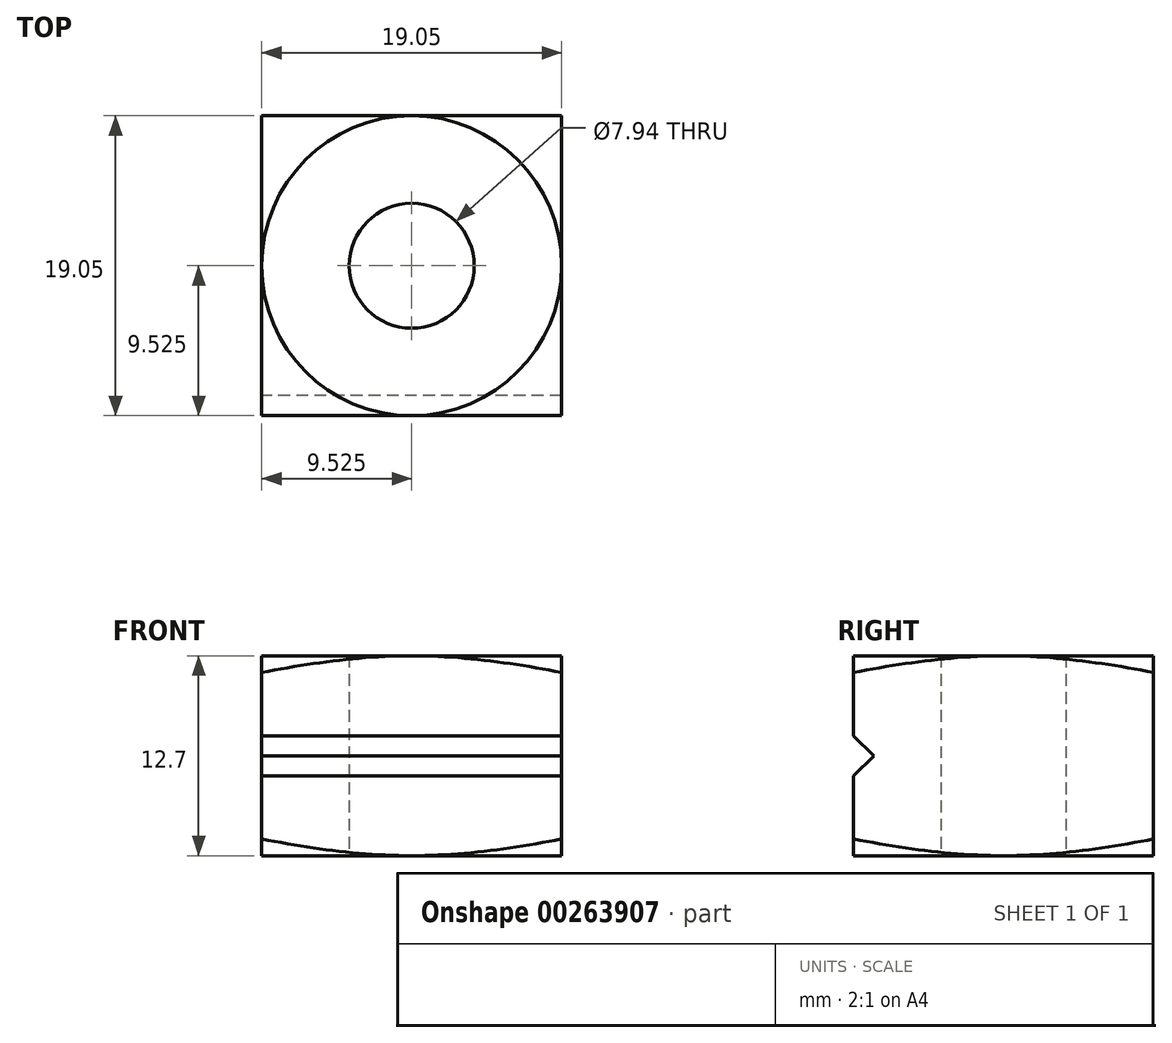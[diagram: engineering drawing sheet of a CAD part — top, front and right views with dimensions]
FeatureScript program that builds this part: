
annotation { "Feature Type Name" : "Feature", "Feature Type Description" : "" }
export const myFeature = defineFeature(function(context is Context, id is Id, definition is map)
    precondition{}
    {
        {
            var Q0;
            Q0=qCreatedBy(makeId("Top.planeOp"),FACE);
            var sketch = newSketch(context, id + "F0", { "sketchPlane" : qUnion([Q0])});
            skLineSegment(sketch, "E0.bottom", {"start": v(0, 0) * mm, "end": v(19.05, 0) * mm});
            skLineSegment(sketch, "E0.top", {"start": v(0, 19.05) * mm, "end": v(19.05, 19.05) * mm});
            skLineSegment(sketch, "E0.left", {"start": v(0, 0) * mm, "end": v(0, 19.05) * mm});
            skLineSegment(sketch, "E0.right", {"start": v(19.05, 0) * mm, "end": v(19.05, 19.05) * mm});
            skSolve(sketch);
        }
        {
            var Q0;
            Q0 = qSketchRegion(id + "F0", true);
            extrude(context, id + "F1", {"entities" : qUnion([Q0]), "depth" : 12.7 * mm});
        }
        {
            var Q0;
            Q0=makeQuery(id+"F1.opExtrude","SWEPT_FACE",FACE,{"disambiguationData":[OSD([sQuery(id+"F0.wireOp",EDGE,"E0.left")])]});
            var sketch = newSketch(context, id + "F2", { "sketchPlane" : qUnion([Q0])});
            skLineSegment(sketch, "E1", {"start": v(-1.27, 6.35) * mm, "end": v(0, 5.08) * mm});
            skPoint(sketch, "E1.startSnap0", {"position": v(0, 6.35) * mm});
            skLineSegment(sketch, "E2", {"start": v(-1.27, 6.35) * mm, "end": v(0, 7.62) * mm});
            skLineSegment(sketch, "E3", {"start": v(0, 7.62) * mm, "end": v(0, 5.08) * mm});
            skLineSegment(sketch, "E4", {"start": v(0, 6.35) * mm, "end": v(-1.27, 6.35) * mm, "construction": true});
            skSolve(sketch);
        }
        {
            var Q0;
            Q0 = qSketchRegion(id + "F2", true);
            extrude(context, id + "F3", {"entities" : qUnion([Q0]), "operationType" : NewBodyOperationType.REMOVE, "oppositeDirection" : true, "depth" : 19.05 * mm});
        }
        {
            var Q0;
            Q0=makeQuery(id+"F1.opExtrude","SWEPT_FACE",FACE,{"disambiguationData":[OSD([sQuery(id+"F0.wireOp",EDGE,"E0.left")])]});
            var Q1;
            Q1=makeQuery(id+"F1.opExtrude","SWEPT_FACE",FACE,{"disambiguationData":[OSD([sQuery(id+"F0.wireOp",EDGE,"E0.right")])]});
            cPlane(context, id + "F4", {"entities" : qUnion([Q0, Q1]), "cplaneType" : CPlaneType.MID_PLANE, "offset" : 25.4 * mm, "width" : 152.4 * mm, "height" : 152.4 * mm});
        }
        {
            var Q0;
            Q0=qCreatedBy(id+"F4.planeOp",FACE);
            var sketch = newSketch(context, id + "F5", { "sketchPlane" : qUnion([Q0])});
            skLineSegment(sketch, "E5", {"start": v(0, 0) * mm, "end": v(8.48, 2.27) * mm});
            skLineSegment(sketch, "E6", {"start": v(8.48, 2.27) * mm, "end": v(8.48, 0) * mm});
            skLineSegment(sketch, "E7", {"start": v(8.48, 0) * mm, "end": v(0, 0) * mm});
            skSolve(sketch);
        }
        {
            var Q0;
            Q0=makeQuery(id+"F1.opExtrude","CAP_FACE",FACE,{"disambiguationData":[OSD([sQuery(id+"F0.wireOp",EDGE,"E0.bottom"),sQuery(id+"F0.wireOp",EDGE,"E0.top"),sQuery(id+"F0.wireOp",EDGE,"E0.left"),sQuery(id+"F0.wireOp",EDGE,"E0.right")])],"isStart":true});
            var sketch = newSketch(context, id + "F6", { "sketchPlane" : qUnion([Q0])});
            skCircle(sketch, "E8", {"center": v(9.52, -9.53) * mm, "radius": 3.97 * mm});
            skPoint(sketch, "E8.centerSnap0", {"position": v(19.05, -9.53) * mm});
            skPoint(sketch, "E8.centerSnap1", {"position": v(9.52, -19.05) * mm});
            skSolve(sketch);
        }
        {
            var Q0;
            Q0 = qSketchRegion(id + "F6", true);
            extrude(context, id + "F7", {"entities" : qUnion([Q0]), "operationType" : NewBodyOperationType.REMOVE, "oppositeDirection" : true, "depth" : 19.05 * mm});
        }
        {
            var Q0;
            Q0=qCreatedBy(id+"F4.planeOp",FACE);
            var sketch = newSketch(context, id + "F8", { "sketchPlane" : qUnion([Q0])});
            skPoint(sketch, "E9.0", {"position": v(0, 12.7) * mm});
            skLineSegment(sketch, "E10", {"start": v(-19.05, 12.7) * mm, "end": v(0, 12.7) * mm, "construction": true});
            skLineSegment(sketch, "E11", {"start": v(-19.05, 12.7) * mm, "end": v(-32.24, 16.24) * mm});
            skLineSegment(sketch, "E12", {"start": v(-32.24, 16.24) * mm, "end": v(-32.24, 9.16) * mm});
            skLineSegment(sketch, "E13", {"start": v(-32.24, 9.16) * mm, "end": v(-19.05, 12.7) * mm});
            skLineSegment(sketch, "E14", {"start": v(-19.05, 12.7) * mm, "end": v(-32.24, 12.7) * mm, "construction": true});
            skSolve(sketch);
        }
        {
            var Q0;
            Q0=makeQuery(id+"F8.imprint","IMPRINT",FACE,{"disambiguationData":[TD([[makeQuery(id+"F8.imprint","IMPRINT",EDGE,{"derivedFrom":sQuery(id+"F8.wireOp",EDGE,"E11")}),1.0]])]});
            var Q1;
            Q1=makeQuery(id+"F5.imprint","IMPRINT",FACE,{"disambiguationData":[TD([[makeQuery(id+"F5.imprint","IMPRINT",EDGE,{"derivedFrom":sQuery(id+"F5.wireOp",EDGE,"E5")}),-1.0]])]});
            var Q2;
            Q2=makeQuery(id+"F7.boolean.opBoolean","INTERSECT",EDGE,{"derivedFrom":[makeQuery(id+"F1.opExtrude","CAP_FACE",FACE,{"disambiguationData":[OSD([sQuery(id+"F0.wireOp",EDGE,"E0.bottom"),sQuery(id+"F0.wireOp",EDGE,"E0.top"),sQuery(id+"F0.wireOp",EDGE,"E0.left"),sQuery(id+"F0.wireOp",EDGE,"E0.right")])],"isStart":false}),makeQuery(id+"F7.opExtrude","SWEPT_FACE",FACE,{"disambiguationData":[OSD([sQuery(id+"F6.wireOp",EDGE,"E8")])]})]});
            revolve(context, id + "F9", {"operationType" : NewBodyOperationType.REMOVE, "entities" : qUnion([Q0, Q1]), "axis" : qUnion([Q2]), "revolveType" : RevolveType.FULL, "oppositeDirection" : true});
        }
    });
